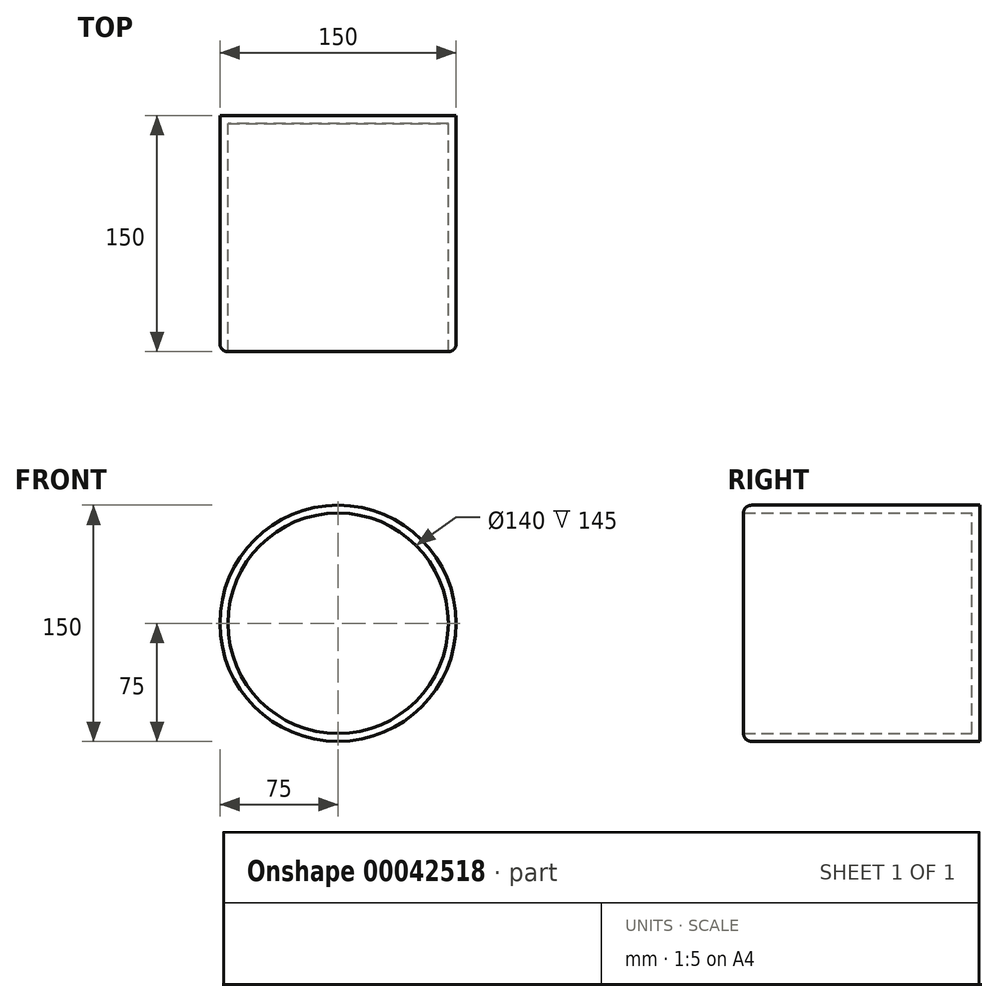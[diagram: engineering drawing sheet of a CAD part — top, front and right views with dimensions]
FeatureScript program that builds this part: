
annotation { "Feature Type Name" : "Feature", "Feature Type Description" : "" }
export const myFeature = defineFeature(function(context is Context, id is Id, definition is map)
    precondition{}
    {
        {
            var Q0;
            Q0=qCreatedBy(makeId("Front.planeOp"),FACE);
            var sketch = newSketch(context, id + "F0", { "sketchPlane" : qUnion([Q0])});
            skCircle(sketch, "E0", {"center": v(0, 0) * mm, "radius": 75 * mm});
            skSolve(sketch);
        }
        {
            var Q0;
            Q0 = qSketchRegion(id + "F0", true);
            extrude(context, id + "F1", {"entities" : qUnion([Q0]), "depth" : 150 * mm});
        }
        {
            var Q0;
            Q0=makeQuery(id+"F1.opExtrude","CAP_FACE",FACE,{"disambiguationData":[OSD([sQuery(id+"F0.wireOp",EDGE,"E0")])],"isStart":false});
            shell(context, id + "F2", {"entities" : qUnion([Q0]), "thickness" : 5 * mm});
        }
        {
            var Q0;
            Q0=makeQuery(id+"F1.opExtrude","CAP_EDGE",EDGE,{"disambiguationData":[OSD([sQuery(id+"F0.wireOp",EDGE,"E0")])],"isStart":false});
            fillet(context, id + "F3", {"entities" : qUnion([Q0]), "radius" : 5 * mm, "tangentPropagation" : true, "allowEdgeOverflow" : false});
        }
    });
